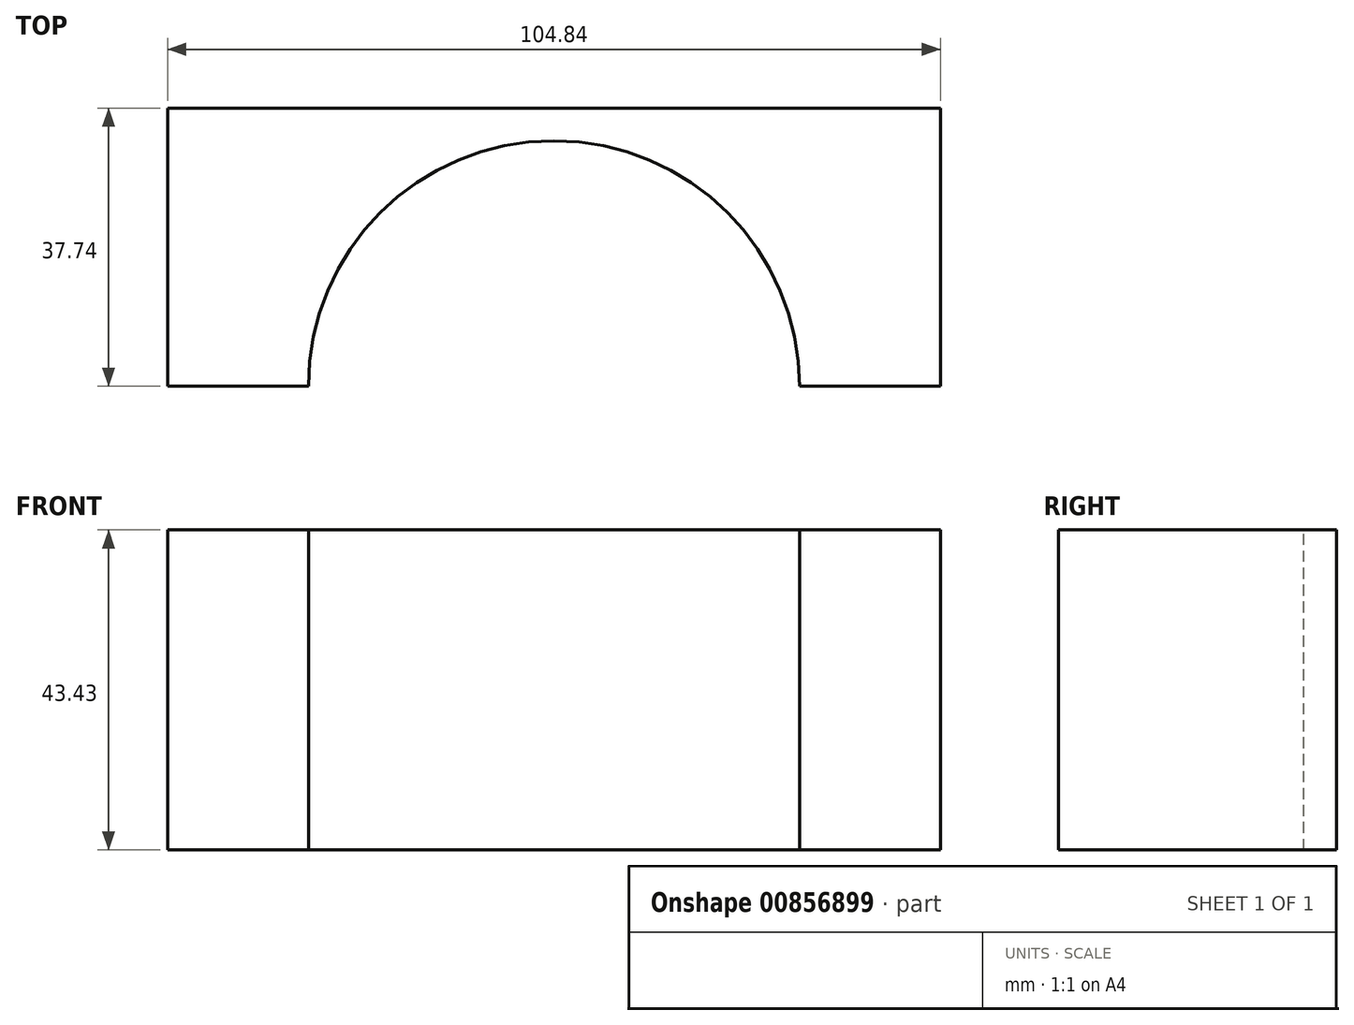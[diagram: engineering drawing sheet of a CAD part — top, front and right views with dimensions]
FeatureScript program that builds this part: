
annotation { "Feature Type Name" : "Feature", "Feature Type Description" : "" }
export const myFeature = defineFeature(function(context is Context, id is Id, definition is map)
    precondition{}
    {
        {
            var Q0;
            Q0=qCreatedBy(makeId("Top.planeOp"),FACE);
            var sketch = newSketch(context, id + "F0", { "sketchPlane" : qUnion([Q0])});
            skLineSegment(sketch, "E0.bottom", {"start": v(-52.42, 37.74) * mm, "end": v(0, 37.74) * mm});
            skLineSegment(sketch, "E0.left", {"start": v(-52.42, 37.74) * mm, "end": v(-52.42, 0) * mm});
            skLineSegment(sketch, "E1.MirrorCS", {"start": v(52.42, 37.74) * mm, "end": v(52.42, 0) * mm});
            skLineSegment(sketch, "E2.MirrorCS", {"start": v(52.42, 37.74) * mm, "end": v(0, 37.74) * mm});
            skLineSegment(sketch, "E3", {"start": v(-52.42, 0) * mm, "end": v(52.42, 0) * mm});
            skSolve(sketch);
        }
        {
            var Q0;
            Q0 = qSketchRegion(id + "F0", true);
            extrude(context, id + "F1", {"entities" : qUnion([Q0]), "depth" : 43.43 * mm, "offsetDistance" : 25.4 * mm});
        }
        {
            var Q0;
            Q0=makeQuery(id+"F1.opExtrude","CAP_FACE",FACE,{"disambiguationData":[OSD([sQuery(id+"F0.wireOp",EDGE,"E0.bottom"),sQuery(id+"F0.wireOp",EDGE,"E0.left"),sQuery(id+"F0.wireOp",EDGE,"E1.MirrorCS"),sQuery(id+"F0.wireOp",EDGE,"E2.MirrorCS"),sQuery(id+"F0.wireOp",EDGE,"E3")])],"isStart":false});
            var sketch = newSketch(context, id + "F2", { "sketchPlane" : qUnion([Q0])});
            skArc(sketch, "E4", {"start": v(33.3, 0) * mm, "mid": v(0, 33.3) * mm, "end": v(-33.3, 0) * mm});
            skLineSegment(sketch, "E5", {"start": v(-33.3, 0) * mm, "end": v(33.3, 0) * mm});
            skSolve(sketch);
        }
        {
            var Q0;
            Q0=makeQuery(id+"F2.imprint","IMPRINT",FACE,{"disambiguationData":[TD([[makeQuery(id+"F2.imprint","IMPRINT",EDGE,{"derivedFrom":sQuery(id+"F2.wireOp",EDGE,"E4")}),1.0]])]});
            extrude(context, id + "F3", {"entities" : qUnion([Q0]), "operationType" : NewBodyOperationType.REMOVE, "endBound" : BoundingType.THROUGH_ALL, "oppositeDirection" : true, "depth" : 25.4 * mm, "offsetDistance" : 25.4 * mm});
        }
    });
